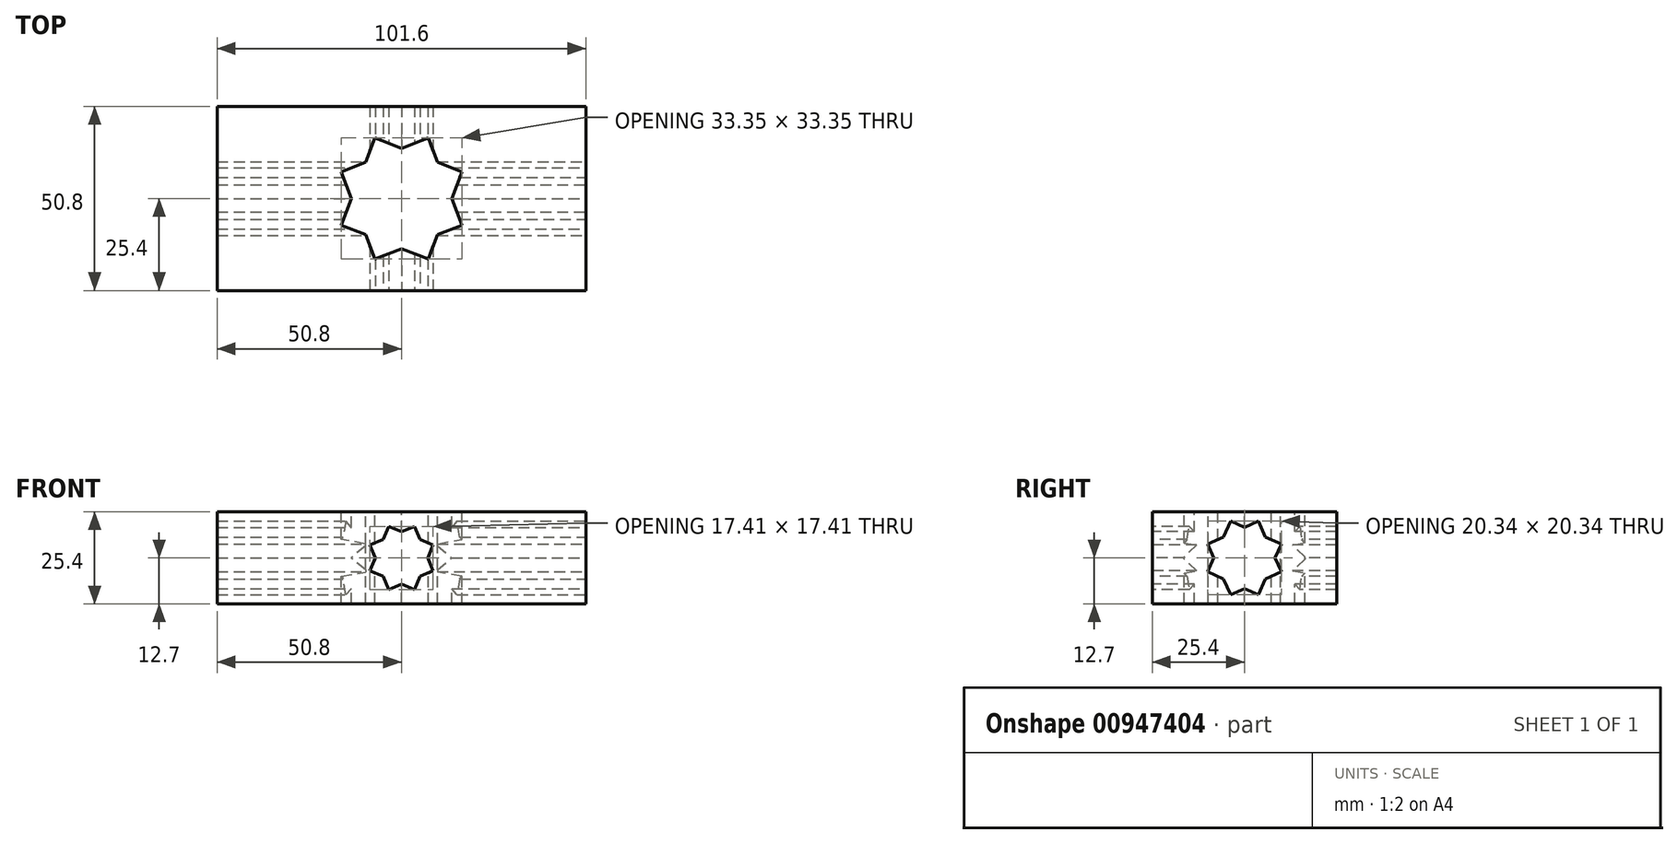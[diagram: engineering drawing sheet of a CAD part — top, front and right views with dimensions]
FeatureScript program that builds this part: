
annotation { "Feature Type Name" : "Feature", "Feature Type Description" : "" }
export const myFeature = defineFeature(function(context is Context, id is Id, definition is map)
    precondition{}
    {
        {
            var Q0;
            Q0=qCreatedBy(makeId("Top.planeOp"),FACE);
            var sketch = newSketch(context, id + "F0", { "sketchPlane" : qUnion([Q0])});
            skLineSegment(sketch, "E0.bottom", {"start": v(-50.8, -25.4) * mm, "end": v(50.8, -25.4) * mm});
            skLineSegment(sketch, "E0.top", {"start": v(-50.8, 25.4) * mm, "end": v(50.8, 25.4) * mm});
            skLineSegment(sketch, "E0.left", {"start": v(-50.8, -25.4) * mm, "end": v(-50.8, 25.4) * mm});
            skLineSegment(sketch, "E0.right", {"start": v(50.8, -25.4) * mm, "end": v(50.8, 25.4) * mm});
            skPoint(sketch, "E0.middle", {"position": v(0, 0) * mm});
            skSolve(sketch);
        }
        {
            var Q0;
            Q0 = qSketchRegion(id + "F0", true);
            extrude(context, id + "F1", {"entities" : qUnion([Q0]), "endBound" : BoundingType.SYMMETRIC, "depth" : 25.4 * mm, "offsetDistance" : 25.4 * mm});
        }
        {
            var Q0;
            Q0=makeQuery(id+"F1.opExtrude","CAP_FACE",FACE,{"disambiguationData":[OSD([sQuery(id+"F0.wireOp",EDGE,"E0.bottom"),sQuery(id+"F0.wireOp",EDGE,"E0.top"),sQuery(id+"F0.wireOp",EDGE,"E0.left"),sQuery(id+"F0.wireOp",EDGE,"E0.right")])],"isStart":false});
            var sketch = newSketch(context, id + "F2", { "sketchPlane" : qUnion([Q0])});
            skCircle(sketch, "E1.cCircle", {"center": v(0, 0) * mm, "radius": 18.22 * mm, "construction": true});
            skLineSegment(sketch, "E1.0", {"start": v(-16.67, -7.34) * mm, "end": v(-7.34, 16.67) * mm});
            skLineSegment(sketch, "E1.1", {"start": v(-7.34, 16.67) * mm, "end": v(16.67, 7.34) * mm});
            skLineSegment(sketch, "E1.2", {"start": v(16.67, 7.34) * mm, "end": v(7.34, -16.67) * mm});
            skLineSegment(sketch, "E1.3", {"start": v(7.34, -16.67) * mm, "end": v(-16.67, -7.34) * mm});
            skLineSegment(sketch, "E2.MirrorCS", {"start": v(-16.67, 7.34) * mm, "end": v(-7.34, -16.67) * mm});
            skLineSegment(sketch, "E3.MirrorCS", {"start": v(-7.34, -16.67) * mm, "end": v(16.67, -7.34) * mm});
            skLineSegment(sketch, "E4.MirrorCS", {"start": v(16.67, -7.34) * mm, "end": v(7.34, 16.67) * mm});
            skLineSegment(sketch, "E5.MirrorCS", {"start": v(7.34, 16.67) * mm, "end": v(-16.67, 7.34) * mm});
            skSolve(sketch);
        }
        {
            var Q0;
            Q0 = qSketchRegion(id + "F2", true);
            extrude(context, id + "F3", {"entities" : qUnion([Q0]), "operationType" : NewBodyOperationType.REMOVE, "oppositeDirection" : true, "depth" : 25.4 * mm, "offsetDistance" : 25.4 * mm});
        }
        {
            var Q0;
            Q0=makeQuery(id+"F1.opExtrude","SWEPT_FACE",FACE,{"disambiguationData":[OSD([sQuery(id+"F0.wireOp",EDGE,"E0.bottom")])]});
            var sketch = newSketch(context, id + "F4", { "sketchPlane" : qUnion([Q0])});
            skCircle(sketch, "E6.cCircle", {"center": v(0, 0) * mm, "radius": 9.4 * mm, "construction": true});
            skLineSegment(sketch, "E6.0", {"start": v(-8.7, -3.57) * mm, "end": v(-3.57, 8.7) * mm});
            skLineSegment(sketch, "E6.1", {"start": v(-3.57, 8.7) * mm, "end": v(8.7, 3.57) * mm});
            skLineSegment(sketch, "E6.2", {"start": v(8.7, 3.57) * mm, "end": v(3.57, -8.7) * mm});
            skLineSegment(sketch, "E6.3", {"start": v(3.57, -8.7) * mm, "end": v(-8.7, -3.57) * mm});
            skLineSegment(sketch, "E7.MirrorCS", {"start": v(-3.57, -8.7) * mm, "end": v(8.7, -3.57) * mm});
            skLineSegment(sketch, "E8.MirrorCS", {"start": v(-8.7, 3.57) * mm, "end": v(-3.57, -8.7) * mm});
            skLineSegment(sketch, "E9.MirrorCS", {"start": v(3.57, 8.7) * mm, "end": v(-8.7, 3.57) * mm});
            skLineSegment(sketch, "E10.MirrorCS", {"start": v(8.7, -3.57) * mm, "end": v(3.57, 8.7) * mm});
            skSolve(sketch);
        }
        {
            var Q0;
            Q0 = qSketchRegion(id + "F4", true);
            extrude(context, id + "F5", {"entities" : qUnion([Q0]), "operationType" : NewBodyOperationType.REMOVE, "oppositeDirection" : true, "depth" : 81.28 * mm, "offsetDistance" : 25.4 * mm});
        }
        {
            var Q0;
            Q0=makeQuery(id+"F1.opExtrude","SWEPT_FACE",FACE,{"disambiguationData":[OSD([sQuery(id+"F0.wireOp",EDGE,"E0.right")])]});
            var sketch = newSketch(context, id + "F6", { "sketchPlane" : qUnion([Q0])});
            skCircle(sketch, "E11.cCircle", {"center": v(0, 0) * mm, "radius": 10.85 * mm, "construction": true});
            skLineSegment(sketch, "E11.0", {"start": v(-10.17, -3.78) * mm, "end": v(-3.78, 10.17) * mm});
            skLineSegment(sketch, "E11.1", {"start": v(-3.78, 10.17) * mm, "end": v(10.17, 3.78) * mm});
            skLineSegment(sketch, "E11.2", {"start": v(10.17, 3.78) * mm, "end": v(3.78, -10.17) * mm});
            skLineSegment(sketch, "E11.3", {"start": v(3.78, -10.17) * mm, "end": v(-10.17, -3.78) * mm});
            skLineSegment(sketch, "E12.MirrorCS", {"start": v(-3.78, -10.17) * mm, "end": v(10.17, -3.78) * mm});
            skLineSegment(sketch, "E13.MirrorCS", {"start": v(-10.17, 3.78) * mm, "end": v(-3.78, -10.17) * mm});
            skLineSegment(sketch, "E14.MirrorCS", {"start": v(3.78, 10.17) * mm, "end": v(-10.17, 3.78) * mm});
            skLineSegment(sketch, "E15.MirrorCS", {"start": v(10.17, -3.78) * mm, "end": v(3.78, 10.17) * mm});
            skSolve(sketch);
        }
        {
            var Q0;
            Q0 = qSketchRegion(id + "F6", true);
            extrude(context, id + "F7", {"entities" : qUnion([Q0]), "operationType" : NewBodyOperationType.REMOVE, "oppositeDirection" : true, "depth" : 125.22 * mm, "offsetDistance" : 25.4 * mm});
        }
    });
